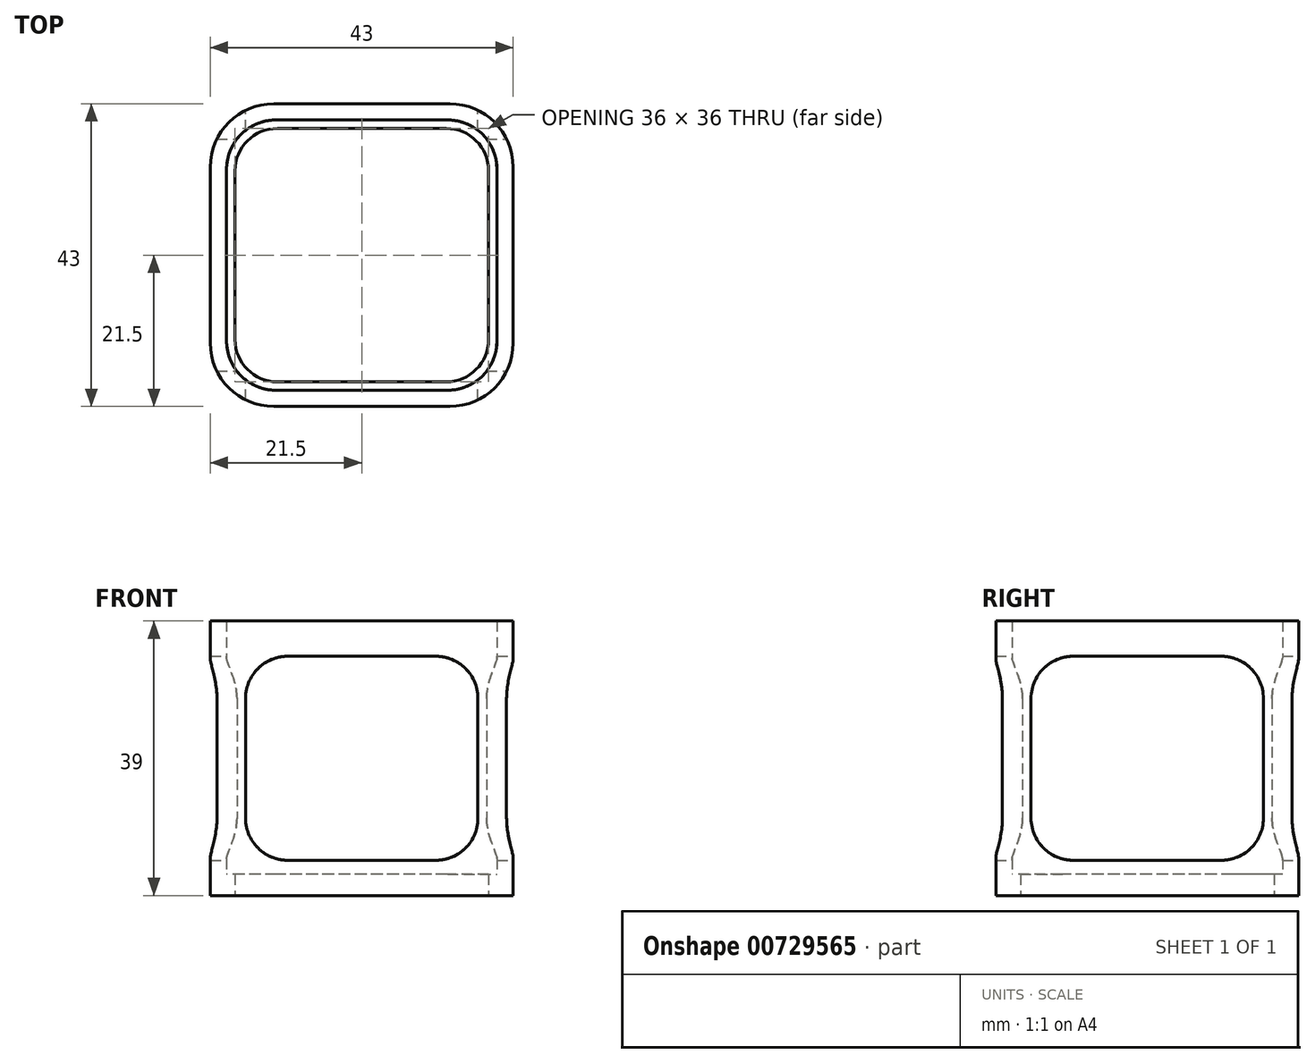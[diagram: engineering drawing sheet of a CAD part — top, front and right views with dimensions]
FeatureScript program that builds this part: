
annotation { "Feature Type Name" : "Feature", "Feature Type Description" : "" }
export const myFeature = defineFeature(function(context is Context, id is Id, definition is map)
    precondition{}
    {
        {
            var Q0;
            Q0=qCreatedBy(makeId("Top.planeOp"),FACE);
            var sketch = newSketch(context, id + "F0", { "sketchPlane" : qUnion([Q0])});
            skLineSegment(sketch, "E0.bottom", {"start": v(12, 18) * mm, "end": v(-12, 18) * mm});
            skLineSegment(sketch, "E0.top", {"start": v(12, -18) * mm, "end": v(-12, -18) * mm});
            skLineSegment(sketch, "E0.left", {"start": v(18, 12) * mm, "end": v(18, -12) * mm});
            skLineSegment(sketch, "E0.right", {"start": v(-18, 12) * mm, "end": v(-18, -12) * mm});
            skPoint(sketch, "E0.middle", {"position": v(0, 0) * mm});
            skPoint(sketch, "E1.visualSharp", {"position": v(-18, 18) * mm});
            skArc(sketch, "E1.filletArc", {"start": v(-12, 18) * mm, "mid": v(-16.24, 16.24) * mm, "end": v(-18, 12) * mm});
            skPoint(sketch, "E2.visualSharp", {"position": v(18, 18) * mm});
            skArc(sketch, "E2.filletArc", {"start": v(18, 12) * mm, "mid": v(16.24, 16.24) * mm, "end": v(12, 18) * mm});
            skPoint(sketch, "E3.visualSharp", {"position": v(-18, -18) * mm});
            skArc(sketch, "E3.filletArc", {"start": v(-18, -12) * mm, "mid": v(-16.24, -16.24) * mm, "end": v(-12, -18) * mm});
            skPoint(sketch, "E4.visualSharp", {"position": v(18, -18) * mm});
            skArc(sketch, "E4.filletArc", {"start": v(12, -18) * mm, "mid": v(16.24, -16.24) * mm, "end": v(18, -12) * mm});
            skLineSegment(sketch, "E5.bottom", {"start": v(12.2, 19.2) * mm, "end": v(-12.2, 19.2) * mm});
            skLineSegment(sketch, "E5.top", {"start": v(12.2, -19.2) * mm, "end": v(-12.2, -19.2) * mm});
            skLineSegment(sketch, "E5.left", {"start": v(19.2, 12.2) * mm, "end": v(19.2, -12.2) * mm});
            skLineSegment(sketch, "E5.right", {"start": v(-19.2, 12.2) * mm, "end": v(-19.2, -12.2) * mm});
            skLineSegment(sketch, "E6.bottom", {"start": v(12.5, 21.5) * mm, "end": v(-12.5, 21.5) * mm});
            skLineSegment(sketch, "E6.top", {"start": v(12.5, -21.5) * mm, "end": v(-12.5, -21.5) * mm});
            skLineSegment(sketch, "E6.left", {"start": v(21.5, 12.5) * mm, "end": v(21.5, -12.5) * mm});
            skLineSegment(sketch, "E6.right", {"start": v(-21.5, 12.5) * mm, "end": v(-21.5, -12.5) * mm});
            skPoint(sketch, "E7.visualSharp", {"position": v(-19.2, 19.2) * mm});
            skArc(sketch, "E7.filletArc", {"start": v(-12.2, 19.2) * mm, "mid": v(-17.15, 17.15) * mm, "end": v(-19.2, 12.2) * mm});
            skPoint(sketch, "E8.visualSharp", {"position": v(19.2, 19.2) * mm});
            skArc(sketch, "E8.filletArc", {"start": v(19.2, 12.2) * mm, "mid": v(17.15, 17.15) * mm, "end": v(12.2, 19.2) * mm});
            skPoint(sketch, "E9.visualSharp", {"position": v(-19.2, -19.2) * mm});
            skArc(sketch, "E9.filletArc", {"start": v(-19.2, -12.2) * mm, "mid": v(-17.15, -17.15) * mm, "end": v(-12.2, -19.2) * mm});
            skPoint(sketch, "E10.visualSharp", {"position": v(19.2, -19.2) * mm});
            skArc(sketch, "E10.filletArc", {"start": v(12.2, -19.2) * mm, "mid": v(17.15, -17.15) * mm, "end": v(19.2, -12.2) * mm});
            skPoint(sketch, "E11.visualSharp", {"position": v(-21.5, -21.5) * mm});
            skArc(sketch, "E11.filletArc", {"start": v(-21.5, -12.5) * mm, "mid": v(-18.86, -18.86) * mm, "end": v(-12.5, -21.5) * mm});
            skPoint(sketch, "E12.visualSharp", {"position": v(21.5, -21.5) * mm});
            skArc(sketch, "E12.filletArc", {"start": v(12.5, -21.5) * mm, "mid": v(18.86, -18.86) * mm, "end": v(21.5, -12.5) * mm});
            skPoint(sketch, "E13.visualSharp", {"position": v(-21.5, 21.5) * mm});
            skArc(sketch, "E13.filletArc", {"start": v(-12.5, 21.5) * mm, "mid": v(-18.86, 18.86) * mm, "end": v(-21.5, 12.5) * mm});
            skPoint(sketch, "E14.visualSharp", {"position": v(21.5, 21.5) * mm});
            skArc(sketch, "E14.filletArc", {"start": v(21.5, 12.5) * mm, "mid": v(18.86, 18.86) * mm, "end": v(12.5, 21.5) * mm});
            skSolve(sketch);
        }
        {
            var Q0;
            Q0=makeQuery(id+"F0.imprint","IMPRINT",FACE,{"disambiguationData":[TD([[makeQuery(id+"F0.imprint","IMPRINT",EDGE,{"derivedFrom":sQuery(id+"F0.wireOp",EDGE,"E0.bottom")}),-1.0]])]});
            extrude(context, id + "F1", {"entities" : qUnion([Q0]), "depth" : 3 * mm, "offsetDistance" : 25 * mm});
        }
        {
            var Q0;
            Q0=makeQuery(id+"F0.imprint","IMPRINT",FACE,{"disambiguationData":[TD([[makeQuery(id+"F0.imprint","IMPRINT",EDGE,{"derivedFrom":sQuery(id+"F0.wireOp",EDGE,"E5.bottom")}),-1.0]])]});
            extrude(context, id + "F2", {"entities" : qUnion([Q0]), "operationType" : NewBodyOperationType.ADD, "depth" : 39 * mm, "offsetDistance" : 25 * mm});
        }
        {
            var Q0;
            Q0=makeQuery(id+"F2.opExtrude","SWEPT_FACE",FACE,{"disambiguationData":[OSD([sQuery(id+"F0.wireOp",EDGE,"E6.bottom")])]});
            var sketch = newSketch(context, id + "F3", { "sketchPlane" : qUnion([Q0])});
            skLineSegment(sketch, "E15", {"start": v(0, 39) * mm, "end": v(0, 0) * mm});
            skLineSegment(sketch, "E16.bottom", {"start": v(10.5, 34) * mm, "end": v(-10.5, 34) * mm});
            skLineSegment(sketch, "E16.top", {"start": v(10.5, 5) * mm, "end": v(-10.5, 5) * mm});
            skLineSegment(sketch, "E16.left", {"start": v(16.5, 28) * mm, "end": v(16.5, 11) * mm});
            skLineSegment(sketch, "E16.right", {"start": v(-16.5, 28) * mm, "end": v(-16.5, 11) * mm});
            skPoint(sketch, "E16.middle", {"position": v(0, 19.5) * mm});
            skPoint(sketch, "E17.visualSharp", {"position": v(-16.5, 34) * mm});
            skArc(sketch, "E17.filletArc", {"start": v(-10.5, 34) * mm, "mid": v(-14.74, 32.24) * mm, "end": v(-16.5, 28) * mm});
            skPoint(sketch, "E18.visualSharp", {"position": v(-16.5, 5) * mm});
            skArc(sketch, "E18.filletArc", {"start": v(-16.5, 11) * mm, "mid": v(-14.74, 6.76) * mm, "end": v(-10.5, 5) * mm});
            skPoint(sketch, "E19.visualSharp", {"position": v(16.5, 5) * mm});
            skArc(sketch, "E19.filletArc", {"start": v(10.5, 5) * mm, "mid": v(14.74, 6.76) * mm, "end": v(16.5, 11) * mm});
            skPoint(sketch, "E20.visualSharp", {"position": v(16.5, 34) * mm});
            skArc(sketch, "E20.filletArc", {"start": v(16.5, 28) * mm, "mid": v(14.74, 32.24) * mm, "end": v(10.5, 34) * mm});
            skSolve(sketch);
        }
        {
            var Q0;
            {var subQ0=sQuery(id+"F3.wireOp",EDGE,"E16.right");Q0=makeQuery(id+"F3.imprint","IMPRINT",FACE,{"disambiguationData":[TD([[makeQuery(id+"F3.imprint","IMPRINT",EDGE,{"derivedFrom":subQ0}),1.0]])]});}
            var Q1;
            {var subQ1=sQuery(id+"F3.wireOp",EDGE,"E16.bottom");var subQ5=sQuery(id+"F3.wireOp",EDGE,"E15");var subQ6=makeQuery(id+"F3.imprint","INTERSECT",VERTEX,{"derivedFrom":[subQ5,subQ1]});Q1=makeQuery(id+"F3.imprint","IMPRINT",FACE,{"disambiguationData":[TD([[makeQuery(id+"F3.imprint","IMPRINT",EDGE,{"disambiguationData":[TD([[subQ6,-1.0]])],"derivedFrom":subQ5}),-1.0]])]});}
            var Q2;
            {var subQ3=sQuery(id+"F3.wireOp",EDGE,"E15");var subQ6=sQuery(id+"F3.wireOp",EDGE,"E16.bottom");var subQ11=makeQuery(id+"F3.imprint","INTERSECT",VERTEX,{"derivedFrom":[subQ3,subQ6]});Q2=makeQuery(id+"F3.imprint","IMPRINT",FACE,{"disambiguationData":[TD([[makeQuery(id+"F3.imprint","IMPRINT",EDGE,{"disambiguationData":[TD([[subQ11,-1.0]])],"derivedFrom":subQ3}),1.0]])]});}
            var Q3;
            {var subQ0=sQuery(id+"F3.wireOp",EDGE,"E16.left");Q3=makeQuery(id+"F3.imprint","IMPRINT",FACE,{"disambiguationData":[TD([[makeQuery(id+"F3.imprint","IMPRINT",EDGE,{"derivedFrom":subQ0}),-1.0]])]});}
            extrude(context, id + "F4", {"entities" : qUnion([Q0, Q1, Q2, Q3]), "operationType" : NewBodyOperationType.REMOVE, "oppositeDirection" : true, "depth" : 43 * mm, "offsetDistance" : 25 * mm});
        }
        {
            var Q0;
            Q0=makeQuery(id+"F2.opExtrude","SWEPT_FACE",FACE,{"disambiguationData":[OSD([sQuery(id+"F0.wireOp",EDGE,"E6.left")])]});
            var sketch = newSketch(context, id + "F5", { "sketchPlane" : qUnion([Q0])});
            skLineSegment(sketch, "E21", {"start": v(0, 39) * mm, "end": v(0, 0) * mm});
            skLineSegment(sketch, "E22.bottom", {"start": v(10.5, 34) * mm, "end": v(-10.5, 34) * mm});
            skLineSegment(sketch, "E22.top", {"start": v(10.5, 5) * mm, "end": v(-10.5, 5) * mm});
            skLineSegment(sketch, "E22.left", {"start": v(16.5, 28) * mm, "end": v(16.5, 11) * mm});
            skLineSegment(sketch, "E22.right", {"start": v(-16.5, 28) * mm, "end": v(-16.5, 11) * mm});
            skPoint(sketch, "E22.middle", {"position": v(0, 19.5) * mm});
            skPoint(sketch, "E23.visualSharp", {"position": v(-16.5, 34) * mm});
            skArc(sketch, "E23.filletArc", {"start": v(-10.5, 34) * mm, "mid": v(-14.74, 32.24) * mm, "end": v(-16.5, 28) * mm});
            skPoint(sketch, "E24.visualSharp", {"position": v(16.5, 34) * mm});
            skArc(sketch, "E24.filletArc", {"start": v(16.5, 28) * mm, "mid": v(14.74, 32.24) * mm, "end": v(10.5, 34) * mm});
            skPoint(sketch, "E25.visualSharp", {"position": v(-16.5, 5) * mm});
            skArc(sketch, "E25.filletArc", {"start": v(-16.5, 11) * mm, "mid": v(-14.74, 6.76) * mm, "end": v(-10.5, 5) * mm});
            skPoint(sketch, "E26.visualSharp", {"position": v(16.5, 5) * mm});
            skArc(sketch, "E26.filletArc", {"start": v(10.5, 5) * mm, "mid": v(14.74, 6.76) * mm, "end": v(16.5, 11) * mm});
            skSolve(sketch);
        }
        {
            var Q0;
            {var subQ0=sQuery(id+"F5.wireOp",EDGE,"E22.right");Q0=makeQuery(id+"F5.imprint","IMPRINT",FACE,{"disambiguationData":[TD([[makeQuery(id+"F5.imprint","IMPRINT",EDGE,{"derivedFrom":subQ0}),1.0]])]});}
            var Q1;
            {var subQ1=sQuery(id+"F5.wireOp",EDGE,"E22.bottom");var subQ5=sQuery(id+"F5.wireOp",EDGE,"E21");var subQ6=makeQuery(id+"F5.imprint","INTERSECT",VERTEX,{"derivedFrom":[subQ5,subQ1]});Q1=makeQuery(id+"F5.imprint","IMPRINT",FACE,{"disambiguationData":[TD([[makeQuery(id+"F5.imprint","IMPRINT",EDGE,{"disambiguationData":[TD([[subQ6,-1.0]])],"derivedFrom":subQ5}),-1.0]])]});}
            var Q2;
            {var subQ1=sQuery(id+"F5.wireOp",EDGE,"E22.bottom");var subQ5=sQuery(id+"F5.wireOp",EDGE,"E21");var subQ6=makeQuery(id+"F5.imprint","INTERSECT",VERTEX,{"derivedFrom":[subQ5,subQ1]});Q2=makeQuery(id+"F5.imprint","IMPRINT",FACE,{"disambiguationData":[TD([[makeQuery(id+"F5.imprint","IMPRINT",EDGE,{"disambiguationData":[TD([[subQ6,-1.0]])],"derivedFrom":subQ5}),1.0]])]});}
            var Q3;
            {var subQ0=sQuery(id+"F5.wireOp",EDGE,"E22.left");Q3=makeQuery(id+"F5.imprint","IMPRINT",FACE,{"disambiguationData":[TD([[makeQuery(id+"F5.imprint","IMPRINT",EDGE,{"derivedFrom":subQ0}),-1.0]])]});}
            extrude(context, id + "F6", {"entities" : qUnion([Q0, Q1, Q2, Q3]), "operationType" : NewBodyOperationType.REMOVE, "oppositeDirection" : true, "depth" : 43 * mm, "offsetDistance" : 25 * mm});
        }
    });
